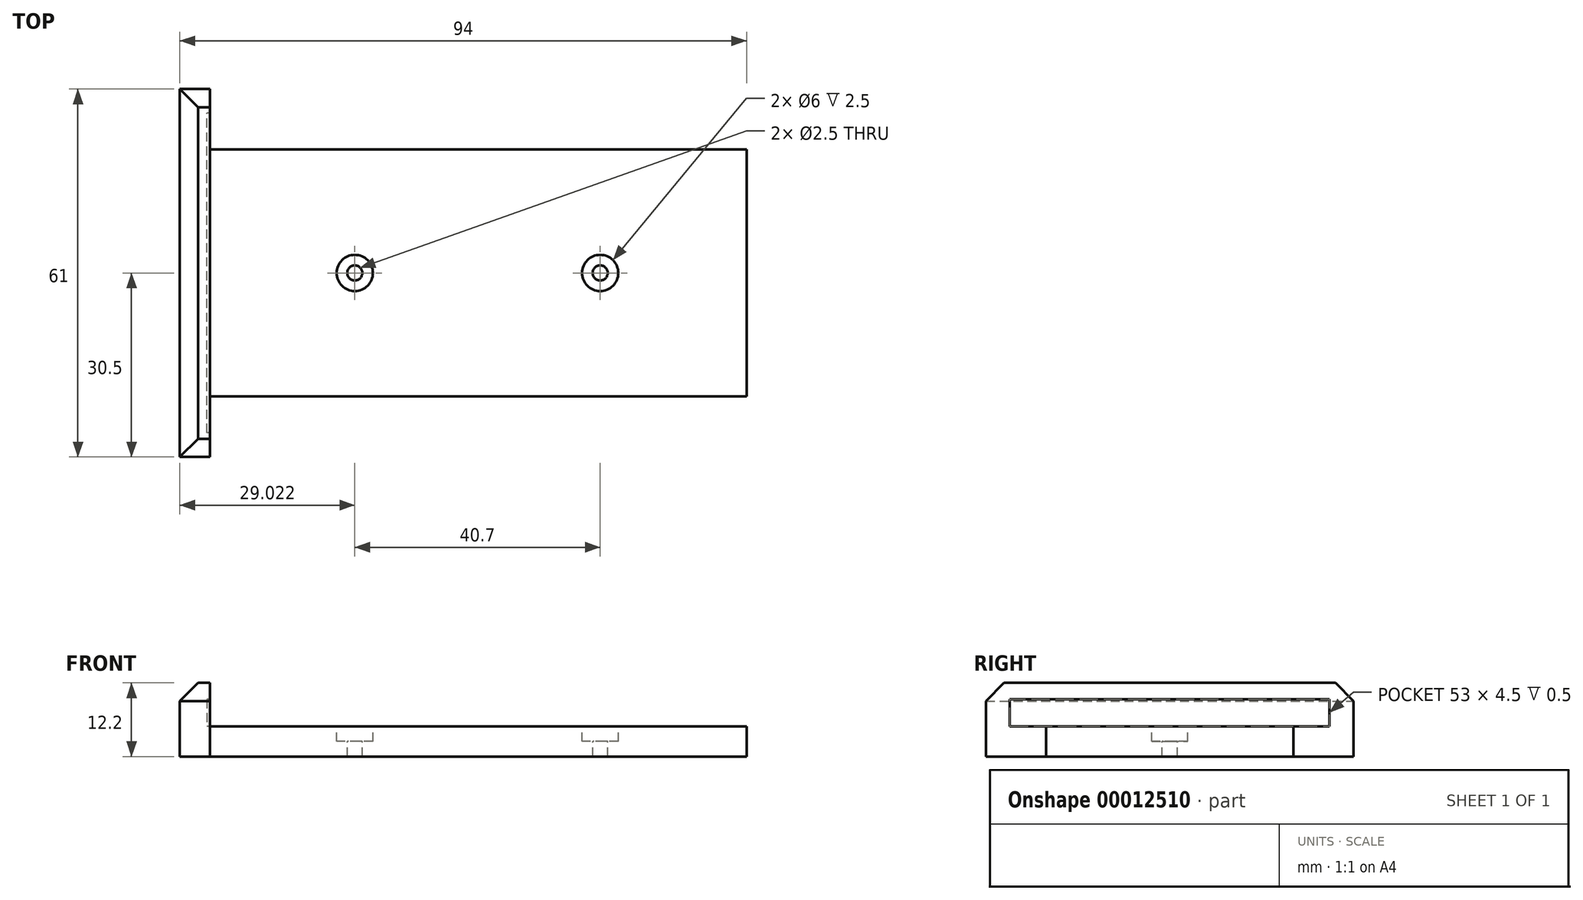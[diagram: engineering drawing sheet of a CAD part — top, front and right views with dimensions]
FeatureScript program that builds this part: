
annotation { "Feature Type Name" : "Feature", "Feature Type Description" : "" }
export const myFeature = defineFeature(function(context is Context, id is Id, definition is map)
    precondition{}
    {
        {
            var Q0;
            Q0=qCreatedBy(makeId("Top.planeOp"),FACE);
            var sketch = newSketch(context, id + "F0", { "sketchPlane" : qUnion([Q0])});
            skLineSegment(sketch, "E0.rect.bottom", {"start": v(44.5, -20.5) * mm, "end": v(-44.5, -20.5) * mm});
            skLineSegment(sketch, "E0.rect.top", {"start": v(44.5, 20.5) * mm, "end": v(-44.5, 20.5) * mm});
            skLineSegment(sketch, "E0.rect.left", {"start": v(44.5, -20.5) * mm, "end": v(44.5, 20.5) * mm});
            skLineSegment(sketch, "E0.rect.right", {"start": v(-44.5, -20.5) * mm, "end": v(-44.5, 20.5) * mm});
            skPoint(sketch, "E0.rect.middle", {"position": v(0, 0) * mm});
            skLineSegment(sketch, "E1.bottom", {"start": v(-44.5, 20.5) * mm, "end": v(44.5, 20.5) * mm});
            skLineSegment(sketch, "E1.top", {"start": v(-44.5, 30.5) * mm, "end": v(44.5, 30.5) * mm});
            skLineSegment(sketch, "E1.left", {"start": v(-44.5, 20.5) * mm, "end": v(-44.5, 30.5) * mm});
            skLineSegment(sketch, "E1.right", {"start": v(44.5, 20.5) * mm, "end": v(44.5, 30.5) * mm});
            skLineSegment(sketch, "E2.bottom", {"start": v(-44.5, -20.5) * mm, "end": v(44.5, -20.5) * mm});
            skLineSegment(sketch, "E2.top", {"start": v(-44.5, -30.5) * mm, "end": v(44.5, -30.5) * mm});
            skLineSegment(sketch, "E2.left", {"start": v(-44.5, -20.5) * mm, "end": v(-44.5, -30.5) * mm});
            skLineSegment(sketch, "E2.right", {"start": v(44.5, -20.5) * mm, "end": v(44.5, -30.5) * mm});
            skLineSegment(sketch, "E3.bottom", {"start": v(-44.5, 30.5) * mm, "end": v(-49.5, 30.5) * mm});
            skLineSegment(sketch, "E3.top", {"start": v(-44.5, -30.5) * mm, "end": v(-49.5, -30.5) * mm});
            skLineSegment(sketch, "E3.left", {"start": v(-44.5, 30.5) * mm, "end": v(-44.5, -30.5) * mm});
            skLineSegment(sketch, "E3.right", {"start": v(-49.5, 30.5) * mm, "end": v(-49.5, -30.5) * mm});
            skSolve(sketch);
        }
        {
            var Q0;
            Q0=makeQuery(id+"F0.imprint","IMPRINT",FACE,{"disambiguationData":[TD([[makeQuery(id+"F0.imprint","IMPRINT",EDGE,{"derivedFrom":sQuery(id+"F0.wireOp",EDGE,"E0.rect.left")}),1.0]])]});
            extrude(context, id + "F1", {"entities" : qUnion([Q0]), "depth" : 5 * mm});
        }
        {
            var Q0;
            {var subQ2=sQuery(id+"F0.wireOp",EDGE,"E2.bottom");Q0=makeQuery(id+"F0.imprint","IMPRINT",FACE,{"disambiguationData":[TD([[makeQuery(id+"F0.imprint","IMPRINT",EDGE,{"derivedFrom":subQ2}),-1.0]])]});}
            var Q1;
            {var subQ2=sQuery(id+"F0.wireOp",EDGE,"E1.bottom");Q1=makeQuery(id+"F0.imprint","IMPRINT",FACE,{"disambiguationData":[TD([[makeQuery(id+"F0.imprint","IMPRINT",EDGE,{"derivedFrom":subQ2}),1.0]])]});}
            var Q2;
            {var subQ4=sQuery(id+"F0.wireOp",EDGE,"E3.bottom");Q2=makeQuery(id+"F0.imprint","IMPRINT",FACE,{"disambiguationData":[TD([[makeQuery(id+"F0.imprint","IMPRINT",EDGE,{"derivedFrom":subQ4}),1.0]])]});}
            extrude(context, id + "F2", {"entities" : qUnion([Q0, Q1, Q2]), "operationType" : NewBodyOperationType.ADD, "depth" : 12.2 * mm});
        }
        {
            var Q0;
            Q0=makeQuery(id+"F1.opExtrude","CAP_FACE",FACE,{"disambiguationData":[OSD([sQuery(id+"F0.wireOp",EDGE,"E0.rect.left"),sQuery(id+"F0.wireOp",EDGE,"E1.bottom"),sQuery(id+"F0.wireOp",EDGE,"E2.bottom"),sQuery(id+"F0.wireOp",EDGE,"E3.left")])],"isStart":false});
            var sketch = newSketch(context, id + "F3", { "sketchPlane" : qUnion([Q0])});
            skLineSegment(sketch, "E4.rect.bottom", {"start": v(45, -26.5) * mm, "end": v(-45, -26.5) * mm});
            skLineSegment(sketch, "E4.rect.top", {"start": v(45, 26.5) * mm, "end": v(-45, 26.5) * mm});
            skLineSegment(sketch, "E4.rect.left", {"start": v(45, -26.5) * mm, "end": v(45, 26.5) * mm});
            skLineSegment(sketch, "E4.rect.right", {"start": v(-45, -26.5) * mm, "end": v(-45, 26.5) * mm});
            skPoint(sketch, "E4.rect.middle", {"position": v(0, 0) * mm});
            skSolve(sketch);
        }
        {
            var Q0;
            Q0 = qSketchRegion(id + "F3", true);
            extrude(context, id + "F4", {"entities" : qUnion([Q0]), "operationType" : NewBodyOperationType.REMOVE, "depth" : 4.5 * mm});
        }
        {
            var Q0;
            Q0=makeQuery(id+"F2.opExtrude","CAP_EDGE",EDGE,{"disambiguationData":[OSD([sQuery(id+"F0.wireOp",EDGE,"E2.top"),sQuery(id+"F0.wireOp",EDGE,"E3.top")])],"isStart":false});
            var Q1;
            Q1=makeQuery(id+"F2.opExtrude","CAP_EDGE",EDGE,{"disambiguationData":[OSD([sQuery(id+"F0.wireOp",EDGE,"E3.right")])],"isStart":false});
            var Q2;
            Q2=makeQuery(id+"F2.opExtrude","CAP_EDGE",EDGE,{"disambiguationData":[OSD([sQuery(id+"F0.wireOp",EDGE,"E1.top"),sQuery(id+"F0.wireOp",EDGE,"E3.bottom")])],"isStart":false});
            chamfer(context, id + "F5", {"entities" : qUnion([Q0, Q1, Q2]), "width" : 3 * mm, "tangentPropagation" : true});
        }
        {
            var Q0;
            Q0=makeQuery(id+"F4.boolean.opBoolean","MERGE",FACE,{"derivedFrom":[makeQuery(id+"F1.opExtrude","CAP_FACE",FACE,{"disambiguationData":[OSD([sQuery(id+"F0.wireOp",EDGE,"E0.rect.left"),sQuery(id+"F0.wireOp",EDGE,"E1.bottom"),sQuery(id+"F0.wireOp",EDGE,"E2.bottom"),sQuery(id+"F0.wireOp",EDGE,"E3.left")])],"isStart":false}),makeQuery(id+"F4.opExtrude","CAP_FACE",FACE,{"disambiguationData":[OSD([sQuery(id+"F3.wireOp",EDGE,"E4.rect.bottom"),sQuery(id+"F3.wireOp",EDGE,"E4.rect.top"),sQuery(id+"F3.wireOp",EDGE,"E4.rect.left"),sQuery(id+"F3.wireOp",EDGE,"E4.rect.right")])],"isStart":true})]});
            var sketch = newSketch(context, id + "F6", { "sketchPlane" : qUnion([Q0])});
            skCircle(sketch, "E5", {"center": v(-20.48, 0) * mm, "radius": 3 * mm});
            skCircle(sketch, "E6", {"center": v(20.22, 0) * mm, "radius": 3 * mm});
            skCircle(sketch, "E7", {"center": v(-20.48, 0) * mm, "radius": 1.25 * mm});
            skCircle(sketch, "E8", {"center": v(20.22, 0) * mm, "radius": 1.25 * mm});
            skSolve(sketch);
        }
        {
            var Q0;
            Q0=makeQuery(id+"F6.imprint","IMPRINT",FACE,{"disambiguationData":[TD([[makeQuery(id+"F6.imprint","IMPRINT",EDGE,{"derivedFrom":sQuery(id+"F6.wireOp",EDGE,"E8")}),1.0]])]});
            var Q1;
            Q1=makeQuery(id+"F6.imprint","IMPRINT",FACE,{"disambiguationData":[TD([[makeQuery(id+"F6.imprint","IMPRINT",EDGE,{"derivedFrom":sQuery(id+"F6.wireOp",EDGE,"E6")}),1.0]])]});
            extrude(context, id + "F7", {"entities" : qUnion([Q0, Q1]), "operationType" : NewBodyOperationType.REMOVE, "oppositeDirection" : true, "depth" : 2.5 * mm});
        }
        {
            var Q0;
            Q0=makeQuery(id+"F6.imprint","IMPRINT",FACE,{"disambiguationData":[TD([[makeQuery(id+"F6.imprint","IMPRINT",EDGE,{"derivedFrom":sQuery(id+"F6.wireOp",EDGE,"E5")}),1.0]])]});
            var Q1;
            Q1=makeQuery(id+"F6.imprint","IMPRINT",FACE,{"disambiguationData":[TD([[makeQuery(id+"F6.imprint","IMPRINT",EDGE,{"derivedFrom":sQuery(id+"F6.wireOp",EDGE,"E7")}),1.0]])]});
            extrude(context, id + "F8", {"entities" : qUnion([Q0, Q1]), "operationType" : NewBodyOperationType.REMOVE, "oppositeDirection" : true, "depth" : 2.5 * mm});
        }
        {
            var Q0;
            Q0=makeQuery(id+"F6.imprint","IMPRINT",FACE,{"disambiguationData":[TD([[makeQuery(id+"F6.imprint","IMPRINT",EDGE,{"derivedFrom":sQuery(id+"F6.wireOp",EDGE,"E7")}),1.0]])]});
            var Q1;
            Q1=sQuery(id+"F6.wireOp",EDGE,"E7");
            extrude(context, id + "F9", {"entities" : qUnion([Q0]), "operationType" : NewBodyOperationType.REMOVE, "surfaceEntities" : qUnion([Q1]), "oppositeDirection" : true, "depth" : 25 * mm});
        }
        {
            var Q0;
            Q0=makeQuery(id+"F6.imprint","IMPRINT",FACE,{"disambiguationData":[TD([[makeQuery(id+"F6.imprint","IMPRINT",EDGE,{"derivedFrom":sQuery(id+"F6.wireOp",EDGE,"E8")}),1.0]])]});
            var Q1;
            Q1=sQuery(id+"F6.wireOp",EDGE,"E8");
            extrude(context, id + "F10", {"entities" : qUnion([Q0]), "operationType" : NewBodyOperationType.REMOVE, "surfaceEntities" : qUnion([Q1]), "oppositeDirection" : true, "depth" : 25 * mm});
        }
    });
